# Revit family: Keilhauer-Tom-Mid_Back_Chair-1
name_source: partatom
category: Furniture
units: mm (PartAtom-declared; Revit-internal decimal feet)

## family parameters
Always vertical = Yes
Cut with Voids When Loaded = No
OmniClass Number = 23.40.20.00
OmniClass Title = General Furniture and Specialties
Room Calculation Point = No
Shared = No
Work Plane-Based = No

## types (6) — shared parameters
Assembly Code = E2020200
Default Elevation = 0"
Depth = 26"
Keynote = 12500
Low Emitting Finish = Yes
Low Emitting Material = Yes
Manufacturer = Keilhauer
Product Documentation Link = https://keilhauer.com
Revit File Built By = https://servex-us.com
Salvage or Reuse = Yes
Type Comments = Tom
URL = https://keilhauer.com
Width = 26 1/2"
zero-valued in all types: Percentage of Recycled Content

## per-type parameters (varying)
| type | 976 | 986 | Arm | Description | L-Base Arm | L-Base Not Arm |
| 9760 | Yes | No | No | Armless Mid Back, Fully Upholstered Slim Back | No | Yes |
| 9761 | Yes | No | Yes | Mid Back, Fully Upholstered Slim Back, Adjustable Arm With Urethane Cap | Yes | No |
| 9762 | Yes | No | Yes | Mid Back, Fully Upholstered Slim Back, Adjustable Arm With Upholstered Cap | Yes | No |
| 9860 | No | Yes | No | Armless Mid Back, Fully Upholstered Border Back | No | Yes |
| 9861 | No | Yes | Yes | Mid Back, Fully Upholstered Border Back, Adjustable Arm With Urethane Cap | Yes | No |
| 9862 | No | Yes | Yes | Mid Back, Fully Upholstered Border Back, Adjustable Arm With Upholstered Cap | Yes | No |

note: column(s) folded — value = type name in every type: Model

## geometry (parser evidence)
native form markers: Sweep x4
no freeform markers — native parametric forms only
